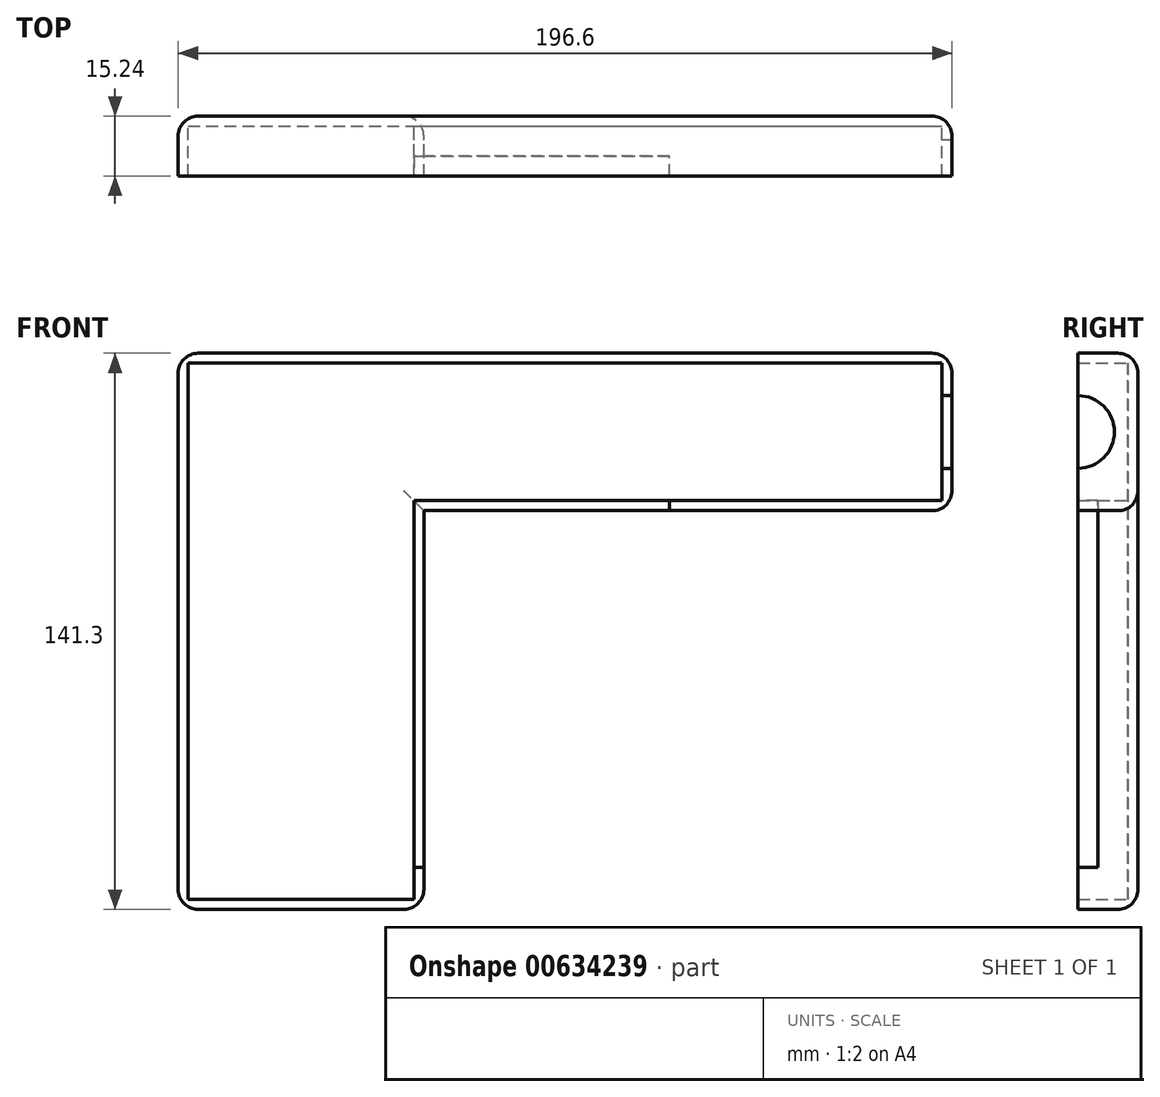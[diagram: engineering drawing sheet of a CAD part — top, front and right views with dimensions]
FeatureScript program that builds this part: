
annotation { "Feature Type Name" : "Feature", "Feature Type Description" : "" }
export const myFeature = defineFeature(function(context is Context, id is Id, definition is map)
    precondition{}
    {
        {
            var Q0;
            Q0=qCreatedBy(makeId("Front.planeOp"),FACE);
            var sketch = newSketch(context, id + "F0", { "sketchPlane" : qUnion([Q0])});
            skLineSegment(sketch, "E0", {"start": v(-94.01, 61.88) * mm, "end": v(102.59, 61.88) * mm});
            skLineSegment(sketch, "E1", {"start": v(-94.01, 61.88) * mm, "end": v(-94.01, -79.42) * mm});
            skLineSegment(sketch, "E2", {"start": v(-94.01, -79.42) * mm, "end": v(-31.61, -79.42) * mm});
            skLineSegment(sketch, "E3", {"start": v(-31.61, -79.42) * mm, "end": v(-31.61, 21.88) * mm});
            skLineSegment(sketch, "E4", {"start": v(-31.61, 21.88) * mm, "end": v(102.59, 21.88) * mm});
            skLineSegment(sketch, "E5", {"start": v(102.59, 21.88) * mm, "end": v(102.59, 61.88) * mm});
            skSolve(sketch);
        }
        {
            var Q0;
            Q0=makeQuery(id+"F0.imprint","IMPRINT",FACE,{"disambiguationData":[TD([[makeQuery(id+"F0.imprint","IMPRINT",EDGE,{"derivedFrom":sQuery(id+"F0.wireOp",EDGE,"E0")}),-1.0]])]});
            extrude(context, id + "F1", {"entities" : qUnion([Q0]), "depth" : 15.24 * mm, "offsetDistance" : 25.4 * mm});
        }
        {
            var Q0;
            Q0=makeQuery(id+"F1.opExtrude","CAP_FACE",FACE,{"disambiguationData":[OSD([sQuery(id+"F0.wireOp",EDGE,"E0"),sQuery(id+"F0.wireOp",EDGE,"E1"),sQuery(id+"F0.wireOp",EDGE,"E2"),sQuery(id+"F0.wireOp",EDGE,"E3"),sQuery(id+"F0.wireOp",EDGE,"E4"),sQuery(id+"F0.wireOp",EDGE,"E5")])],"isStart":false});
            shell(context, id + "F2", {"entities" : qUnion([Q0]), "thickness" : 2.54 * mm});
        }
        {
            var Q0;
            Q0=makeQuery(id+"F1.opExtrude","SWEPT_EDGE",EDGE,{"disambiguationData":[OSD([sQuery(id+"F0.wireOp",EDGE,"E0"),sQuery(id+"F0.wireOp",EDGE,"E1")])]});
            var Q1;
            Q1=makeQuery(id+"F1.opExtrude","SWEPT_EDGE",EDGE,{"disambiguationData":[OSD([sQuery(id+"F0.wireOp",EDGE,"E0"),sQuery(id+"F0.wireOp",EDGE,"E5")])]});
            var Q2;
            Q2=makeQuery(id+"F1.opExtrude","SWEPT_EDGE",EDGE,{"disambiguationData":[OSD([sQuery(id+"F0.wireOp",EDGE,"E4"),sQuery(id+"F0.wireOp",EDGE,"E5")])]});
            var Q3;
            Q3=makeQuery(id+"F1.opExtrude","SWEPT_EDGE",EDGE,{"disambiguationData":[OSD([sQuery(id+"F0.wireOp",EDGE,"E2"),sQuery(id+"F0.wireOp",EDGE,"E3")])]});
            var Q4;
            Q4=makeQuery(id+"F1.opExtrude","SWEPT_EDGE",EDGE,{"disambiguationData":[OSD([sQuery(id+"F0.wireOp",EDGE,"E1"),sQuery(id+"F0.wireOp",EDGE,"E2")])]});
            var Q5;
            Q5=makeQuery(id+"F1.opExtrude","CAP_EDGE",EDGE,{"disambiguationData":[OSD([sQuery(id+"F0.wireOp",EDGE,"E1")])],"isStart":true});
            var Q6;
            Q6=makeQuery(id+"F1.opExtrude","CAP_EDGE",EDGE,{"disambiguationData":[OSD([sQuery(id+"F0.wireOp",EDGE,"E3")])],"isStart":true});
            var Q7;
            Q7=makeQuery(id+"F1.opExtrude","CAP_EDGE",EDGE,{"disambiguationData":[OSD([sQuery(id+"F0.wireOp",EDGE,"E4")])],"isStart":true});
            var Q8;
            Q8=makeQuery(id+"F1.opExtrude","CAP_EDGE",EDGE,{"disambiguationData":[OSD([sQuery(id+"F0.wireOp",EDGE,"E0")])],"isStart":true});
            var Q9;
            Q9=makeQuery(id+"F1.opExtrude","CAP_EDGE",EDGE,{"disambiguationData":[OSD([sQuery(id+"F0.wireOp",EDGE,"E2")])],"isStart":true});
            var Q10;
            Q10=makeQuery(id+"F1.opExtrude","CAP_EDGE",EDGE,{"disambiguationData":[OSD([sQuery(id+"F0.wireOp",EDGE,"E5")])],"isStart":true});
            fillet(context, id + "F3", {"entities" : qUnion([Q0, Q1, Q2, Q3, Q4, Q5, Q6, Q7, Q8, Q9, Q10]), "radius" : 5.08 * mm, "tangentPropagation" : true, "allowEdgeOverflow" : false});
        }
        {
            var Q0;
            Q0=makeQuery(id+"F1.opExtrude","SWEPT_FACE",FACE,{"disambiguationData":[OSD([sQuery(id+"F0.wireOp",EDGE,"E5")])]});
            var sketch = newSketch(context, id + "F4", { "sketchPlane" : qUnion([Q0])});
            skCircle(sketch, "E6", {"center": v(-15.24, 41.88) * mm, "radius": 9.23 * mm});
            skSolve(sketch);
        }
        {
            var Q0;
            Q0=sQuery(id+"F4.wireOp",VERTEX,"E6.center");
            var Q1;
            Q1=makeQuery(id+"F1.opExtrude","SWEPT_BODY",BODY,{"disambiguationData":[OSD([sQuery(id+"F0.wireOp",EDGE,"E0"),sQuery(id+"F0.wireOp",EDGE,"E1"),sQuery(id+"F0.wireOp",EDGE,"E2"),sQuery(id+"F0.wireOp",EDGE,"E3"),sQuery(id+"F0.wireOp",EDGE,"E4"),sQuery(id+"F0.wireOp",EDGE,"E5")])]});
            hole(context, id + "F5", {"style" : HoleStyle.SIMPLE, "endStyle" : HoleEndStyle.BLIND, "holeDiameter" : 18.47 * mm, "majorDiameter" : 6.35 * mm, "holeDepth" : 14 * mm, "isTappedThrough" : true, "tappedDepth" : 12.7 * mm, "tapClearance" : 3, "startFromSketch" : true, "locations" : qUnion([Q0]), "scope" : qUnion([Q1])});
        }
        {
            var Q0;
            Q0=makeQuery(id+"F1.opExtrude","SWEPT_FACE",FACE,{"disambiguationData":[OSD([sQuery(id+"F0.wireOp",EDGE,"E3")])]});
            var sketch = newSketch(context, id + "F6", { "sketchPlane" : qUnion([Q0])});
            skLineSegment(sketch, "E7.bottom", {"start": v(-15.24, 21.88) * mm, "end": v(-10.16, 21.88) * mm});
            skLineSegment(sketch, "E7.top", {"start": v(-15.24, -68.8) * mm, "end": v(-10.16, -68.8) * mm});
            skLineSegment(sketch, "E7.left", {"start": v(-15.24, 21.88) * mm, "end": v(-15.24, -68.8) * mm});
            skLineSegment(sketch, "E7.right", {"start": v(-10.16, 21.88) * mm, "end": v(-10.16, -68.8) * mm});
            skSolve(sketch);
        }
        {
            var Q0;
            Q0 = qSketchRegion(id + "F6", true);
            extrude(context, id + "F7", {"entities" : qUnion([Q0]), "operationType" : NewBodyOperationType.REMOVE, "oppositeDirection" : true, "depth" : 43.69 * mm, "offsetDistance" : 25.4 * mm});
        }
        {
            var Q0;
            Q0=makeQuery(id+"F7.boolean.opBoolean","MERGE",FACE,{"derivedFrom":[makeQuery(id+"F1.opExtrude","SWEPT_FACE",FACE,{"disambiguationData":[OSD([sQuery(id+"F0.wireOp",EDGE,"E4")])]}),makeQuery(id+"F7.opExtrude","SWEPT_FACE",FACE,{"disambiguationData":[OSD([sQuery(id+"F6.wireOp",EDGE,"E7.bottom")])]})]});
            var sketch = newSketch(context, id + "F8", { "sketchPlane" : qUnion([Q0])});
            skLineSegment(sketch, "E8.bottom", {"start": v(-34.15, 15.24) * mm, "end": v(30.79, 15.24) * mm});
            skLineSegment(sketch, "E8.top", {"start": v(-34.15, 10.16) * mm, "end": v(30.79, 10.16) * mm});
            skLineSegment(sketch, "E8.left", {"start": v(-34.15, 15.24) * mm, "end": v(-34.15, 10.16) * mm});
            skLineSegment(sketch, "E8.right", {"start": v(30.79, 15.24) * mm, "end": v(30.79, 10.16) * mm});
            skSolve(sketch);
        }
        {
            var Q0;
            Q0 = qSketchRegion(id + "F8", true);
            extrude(context, id + "F9", {"entities" : qUnion([Q0]), "operationType" : NewBodyOperationType.REMOVE, "oppositeDirection" : true, "depth" : 25.4 * mm, "offsetDistance" : 25.4 * mm});
        }
    });
